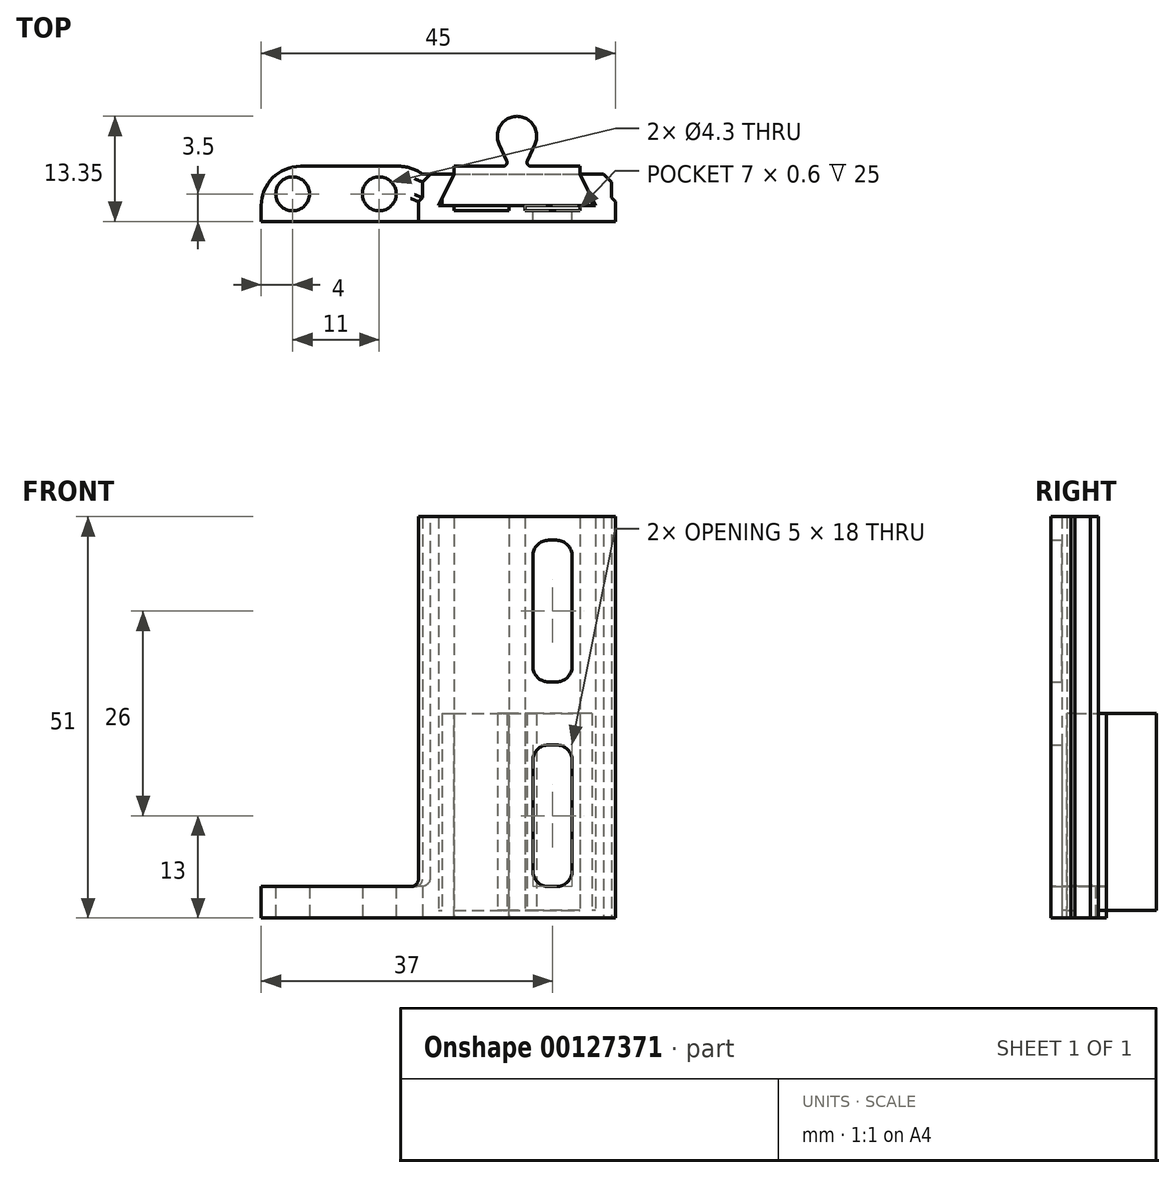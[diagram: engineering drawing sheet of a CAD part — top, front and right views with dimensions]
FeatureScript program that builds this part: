
annotation { "Feature Type Name" : "Feature", "Feature Type Description" : "" }
export const myFeature = defineFeature(function(context is Context, id is Id, definition is map)
    precondition{}
    {
        {
            var Q0;
            Q0=qCreatedBy(makeId("Top.planeOp"),FACE);
            var sketch = newSketch(context, id + "F0", { "sketchPlane" : qUnion([Q0])});
            skLineSegment(sketch, "E0.bottom", {"start": v(0, 0) * mm, "end": v(-2, 0) * mm});
            skLineSegment(sketch, "E0.top", {"start": v(0, -4) * mm, "end": v(-2, -4) * mm, "construction": true});
            skLineSegment(sketch, "E0.left", {"start": v(0, 0) * mm, "end": v(0, -4) * mm, "construction": true});
            skLineSegment(sketch, "E0.right", {"start": v(-2, 0) * mm, "end": v(-2, -4) * mm, "construction": true});
            skLineSegment(sketch, "E1", {"start": v(0, -4) * mm, "end": v(-2, 0) * mm});
            skLineSegment(sketch, "E2.bottom", {"start": v(0, 0) * mm, "end": v(2, 0) * mm});
            skLineSegment(sketch, "E2.top", {"start": v(0, -4) * mm, "end": v(2, -4) * mm});
            skLineSegment(sketch, "E2.right", {"start": v(2, 0) * mm, "end": v(2, -4) * mm});
            skLineSegment(sketch, "E3", {"start": v(-10, 5.55) * mm, "end": v(-10, -8.29) * mm, "construction": true});
            skLineSegment(sketch, "E4.MirrorCS", {"start": v(-20, -4) * mm, "end": v(-18, 0) * mm});
            skLineSegment(sketch, "E5.MirrorCS", {"start": v(-20, 0) * mm, "end": v(-18, 0) * mm});
            skLineSegment(sketch, "E6.MirrorCS", {"start": v(-20, 0) * mm, "end": v(-22, 0) * mm});
            skLineSegment(sketch, "E7.MirrorCS", {"start": v(-22, 0) * mm, "end": v(-22, -4) * mm});
            skLineSegment(sketch, "E8.MirrorCS", {"start": v(-20, -4) * mm, "end": v(-22, -4) * mm});
            skLineSegment(sketch, "E9.bottom", {"start": v(-22.5, -4) * mm, "end": v(2.5, -4) * mm});
            skLineSegment(sketch, "E9.top", {"start": v(-22.5, -6) * mm, "end": v(2.5, -6) * mm});
            skLineSegment(sketch, "E9.left", {"start": v(-22.5, -4) * mm, "end": v(-22.5, -6) * mm});
            skLineSegment(sketch, "E9.right", {"start": v(2.5, -4) * mm, "end": v(2.5, -6) * mm});
            skLineSegment(sketch, "E10", {"start": v(-10, -4) * mm, "end": v(-10, -6) * mm, "construction": true});
            skLineSegment(sketch, "E11", {"start": v(-18, 0) * mm, "end": v(-2, 0) * mm});
            skLineSegment(sketch, "E12.top", {"start": v(-18, 1) * mm, "end": v(-11.78, 1) * mm});
            skLineSegment(sketch, "E12.left", {"start": v(-18, 0) * mm, "end": v(-18, 1) * mm});
            skLineSegment(sketch, "E12.right", {"start": v(-2, 0) * mm, "end": v(-2, 1) * mm});
            skCircle(sketch, "E13", {"center": v(-10, 4.85) * mm, "radius": 2.5 * mm});
            skLineSegment(sketch, "E14", {"start": v(-11.32, 1.7) * mm, "end": v(-12.28, 3.81) * mm});
            skPoint(sketch, "E15.newPointA", {"position": v(-11, 1) * mm});
            skPoint(sketch, "E15.newPointB", {"position": v(-2, 1) * mm});
            skArc(sketch, "E15.filletArc", {"start": v(-11.78, 1) * mm, "mid": v(-11.36, 1.23) * mm, "end": v(-11.32, 1.7) * mm});
            skLineSegment(sketch, "E16.MirrorCS", {"start": v(-8.68, 1.7) * mm, "end": v(-7.72, 3.81) * mm});
            skArc(sketch, "E17.MirrorCS", {"start": v(-8.22, 1) * mm, "mid": v(-8.64, 1.23) * mm, "end": v(-8.68, 1.7) * mm});
            skLineSegment(sketch, "E18.MirrorCS", {"start": v(-2, 1) * mm, "end": v(-8.22, 1) * mm});
            skLineSegment(sketch, "E19", {"start": v(-0.5, -3) * mm, "end": v(-0.5, -4) * mm});
            skLineSegment(sketch, "E20.MirrorCS", {"start": v(-19.5, -3) * mm, "end": v(-19.5, -4) * mm});
            skLineSegment(sketch, "E21.bottom", {"start": v(-18, -4) * mm, "end": v(-11, -4) * mm});
            skLineSegment(sketch, "E21.top", {"start": v(-18, -4.6) * mm, "end": v(-11, -4.6) * mm});
            skLineSegment(sketch, "E21.left", {"start": v(-18, -4) * mm, "end": v(-18, -4.6) * mm});
            skLineSegment(sketch, "E21.right", {"start": v(-11, -4) * mm, "end": v(-11, -4.6) * mm});
            skLineSegment(sketch, "E22.MirrorCS", {"start": v(-9, -4) * mm, "end": v(-9, -4.6) * mm});
            skLineSegment(sketch, "E23.MirrorCS", {"start": v(-2, -4.6) * mm, "end": v(-9, -4.6) * mm});
            skLineSegment(sketch, "E24.MirrorCS", {"start": v(-2, -4) * mm, "end": v(-2, -4.6) * mm});
            skLineSegment(sketch, "E25", {"start": v(-22.5, -6) * mm, "end": v(-42.5, -6) * mm});
            skLineSegment(sketch, "E26", {"start": v(-42.5, -6) * mm, "end": v(-42.5, 1) * mm});
            skLineSegment(sketch, "E27", {"start": v(-42.5, 1) * mm, "end": v(-22, 1) * mm});
            skLineSegment(sketch, "E28", {"start": v(-22, 1) * mm, "end": v(-22, 0) * mm});
            skCircle(sketch, "E29", {"center": v(-38.5, -2.5) * mm, "radius": 2.15 * mm});
            skPoint(sketch, "E29.centerSnap0", {"position": v(-42.5, -2.5) * mm});
            skCircle(sketch, "E30", {"center": v(-27.5, -2.5) * mm, "radius": 2.15 * mm});
            skSolve(sketch);
        }
        {
            var Q0;
            Q0=makeQuery(id+"F0.imprint","IMPRINT",FACE,{"disambiguationData":[TD([[makeQuery(id+"F0.imprint","IMPRINT",EDGE,{"derivedFrom":sQuery(id+"F0.wireOp",EDGE,"E0.bottom")}),1.0]])]});
            var Q1;
            {var subQ1=sQuery(id+"F0.wireOp",EDGE,"E4.MirrorCS");Q1=makeQuery(id+"F0.imprint","IMPRINT",FACE,{"disambiguationData":[TD([[makeQuery(id+"F0.imprint","IMPRINT",EDGE,{"derivedFrom":subQ1}),1.0]])]});}
            var Q2;
            Q2=makeQuery(id+"F0.imprint","IMPRINT",FACE,{"disambiguationData":[TD([[makeQuery(id+"F0.imprint","IMPRINT",EDGE,{"derivedFrom":sQuery(id+"F0.wireOp",EDGE,"E9.top")}),1.0]])]});
            extrude(context, id + "F1", {"entities" : qUnion([Q0, Q1, Q2]), "depth" : 50 * mm});
        }
        {
            var Q0;
            {var subQ1=sQuery(id+"F0.wireOp",EDGE,"E0.bottom");Q0=makeQuery(id+"F0.imprint","IMPRINT",FACE,{"disambiguationData":[TD([[makeQuery(id+"F0.imprint","IMPRINT",EDGE,{"derivedFrom":subQ1}),1.0]])]});}
            var Q1;
            Q1=makeQuery(id+"F1.opExtrude","CAP_FACE",FACE,{"disambiguationData":[OSD([sQuery(id+"F0.wireOp",EDGE,"E0.bottom"),sQuery(id+"F0.wireOp",EDGE,"E1"),sQuery(id+"F0.wireOp",EDGE,"E2.bottom"),sQuery(id+"F0.wireOp",EDGE,"E2.right"),sQuery(id+"F0.wireOp",EDGE,"E4.MirrorCS"),sQuery(id+"F0.wireOp",EDGE,"E5.MirrorCS"),sQuery(id+"F0.wireOp",EDGE,"E6.MirrorCS"),sQuery(id+"F0.wireOp",EDGE,"E7.MirrorCS"),sQuery(id+"F0.wireOp",EDGE,"E9.bottom"),sQuery(id+"F0.wireOp",EDGE,"E9.top"),sQuery(id+"F0.wireOp",EDGE,"E9.left"),sQuery(id+"F0.wireOp",EDGE,"E9.right")])],"isStart":true});
            var Q2;
            {var subQ0=sQuery(id+"F0.wireOp",EDGE,"E11");Q2=makeQuery(id+"F0.imprint","IMPRINT",FACE,{"disambiguationData":[TD([[makeQuery(id+"F0.imprint","IMPRINT",EDGE,{"derivedFrom":subQ0}),-1.0]])]});}
            var Q3;
            {var subQ3=sQuery(id+"F0.wireOp",EDGE,"E19");Q3=makeQuery(id+"F0.imprint","IMPRINT",FACE,{"disambiguationData":[TD([[makeQuery(id+"F0.imprint","IMPRINT",EDGE,{"derivedFrom":subQ3}),1.0]])]});}
            var Q4;
            {var subQ3=sQuery(id+"F0.wireOp",EDGE,"E20.MirrorCS");Q4=makeQuery(id+"F0.imprint","IMPRINT",FACE,{"disambiguationData":[TD([[makeQuery(id+"F0.imprint","IMPRINT",EDGE,{"derivedFrom":subQ3}),-1.0]])]});}
            var Q5;
            {var subQ0=sQuery(id+"F0.wireOp",EDGE,"E22.MirrorCS");Q5=makeQuery(id+"F0.imprint","IMPRINT",FACE,{"disambiguationData":[TD([[makeQuery(id+"F0.imprint","IMPRINT",EDGE,{"derivedFrom":subQ0}),1.0]])]});}
            var Q6;
            Q6=makeQuery(id+"F0.imprint","IMPRINT",FACE,{"disambiguationData":[TD([[makeQuery(id+"F0.imprint","IMPRINT",EDGE,{"derivedFrom":sQuery(id+"F0.wireOp",EDGE,"E21.bottom")}),-1.0]])]});
            extrude(context, id + "F2", {"entities" : qUnion([Q0, Q1, Q2, Q3, Q4, Q5, Q6]), "operationType" : NewBodyOperationType.ADD, "oppositeDirection" : true, "depth" : 1 * mm});
        }
        {
            var Q0;
            Q0=makeQuery(id+"F1.opExtrude","SWEPT_EDGE",EDGE,{"disambiguationData":[OSD([sQuery(id+"F0.wireOp",EDGE,"E7.MirrorCS"),sQuery(id+"F0.wireOp",EDGE,"E9.bottom")])]});
            var Q1;
            Q1=makeQuery(id+"F1.opExtrude","SWEPT_EDGE",EDGE,{"disambiguationData":[OSD([sQuery(id+"F0.wireOp",EDGE,"E2.right"),sQuery(id+"F0.wireOp",EDGE,"E9.bottom")])]});
            var Q2;
            Q2=makeQuery(id+"F1.opExtrude","SWEPT_EDGE",EDGE,{"disambiguationData":[OSD([sQuery(id+"F0.wireOp",EDGE,"E6.MirrorCS"),sQuery(id+"F0.wireOp",EDGE,"E7.MirrorCS")])]});
            var Q3;
            Q3=makeQuery(id+"F1.opExtrude","SWEPT_EDGE",EDGE,{"disambiguationData":[OSD([sQuery(id+"F0.wireOp",EDGE,"E2.bottom"),sQuery(id+"F0.wireOp",EDGE,"E2.right")])]});
            chamfer(context, id + "F3", {"entities" : qUnion([Q0, Q1, Q2, Q3]), "width" : 1 * mm, "tangentPropagation" : true});
        }
        {
            var Q0;
            {var subQ0=sQuery(id+"F0.wireOp",EDGE,"E9.bottom");Q0=makeQuery(id+"F1.opExtrude","SWEPT_FACE",FACE,{"disambiguationData":[OSD([subQ0]),TDD([makeQuery(id+"F0.imprint","IMPRINT",EDGE,{"disambiguationData":[TD([[makeQuery(id+"F0.imprint","INTERSECT",VERTEX,{"derivedFrom":[sQuery(id+"F0.wireOp",EDGE,"E1"),subQ0]}),1.0]])],"derivedFrom":subQ0})])]});}
            var sketch = newSketch(context, id + "F4", { "sketchPlane" : qUnion([Q0])});
            skLineSegment(sketch, "E31.bottom", {"start": v(6, 47) * mm, "end": v(5, 47) * mm});
            skLineSegment(sketch, "E31.top", {"start": v(6, 29) * mm, "end": v(5, 29) * mm});
            skLineSegment(sketch, "E31.left", {"start": v(8, 45) * mm, "end": v(8, 31) * mm});
            skLineSegment(sketch, "E31.right", {"start": v(3, 45) * mm, "end": v(3, 31) * mm});
            skPoint(sketch, "E32.visualSharp", {"position": v(3, 47) * mm});
            skArc(sketch, "E32.filletArc", {"start": v(5, 47) * mm, "mid": v(3.59, 46.41) * mm, "end": v(3, 45) * mm});
            skPoint(sketch, "E33.visualSharp", {"position": v(3, 29) * mm});
            skArc(sketch, "E33.filletArc", {"start": v(3, 31) * mm, "mid": v(3.59, 29.59) * mm, "end": v(5, 29) * mm});
            skPoint(sketch, "E34.visualSharp", {"position": v(8, 29) * mm});
            skArc(sketch, "E34.filletArc", {"start": v(6, 29) * mm, "mid": v(7.41, 29.59) * mm, "end": v(8, 31) * mm});
            skPoint(sketch, "E35.visualSharp", {"position": v(8, 47) * mm});
            skArc(sketch, "E35.filletArc", {"start": v(8, 45) * mm, "mid": v(7.41, 46.41) * mm, "end": v(6, 47) * mm});
            skLineSegment(sketch, "E36", {"start": v(5.5, 29) * mm, "end": v(5.5, 34.69) * mm, "construction": true});
            skLineSegment(sketch, "E37", {"start": v(20, 25) * mm, "end": v(7.35, 25) * mm, "construction": true});
            skPoint(sketch, "E37.endSnap0", {"position": v(20, 25) * mm});
            skLineSegment(sketch, "E38.MirrorCS", {"start": v(6, 21) * mm, "end": v(5, 21) * mm});
            skArc(sketch, "E39.MirrorCS", {"start": v(6, 21) * mm, "mid": v(7.41, 20.41) * mm, "end": v(8, 19) * mm});
            skLineSegment(sketch, "E40.MirrorCS", {"start": v(8, 5) * mm, "end": v(8, 19) * mm});
            skArc(sketch, "E41.MirrorCS", {"start": v(8, 5) * mm, "mid": v(7.41, 3.59) * mm, "end": v(6, 3) * mm});
            skLineSegment(sketch, "E42.MirrorCS", {"start": v(6, 3) * mm, "end": v(5, 3) * mm});
            skArc(sketch, "E43.MirrorCS", {"start": v(5, 3) * mm, "mid": v(3.59, 3.59) * mm, "end": v(3, 5) * mm});
            skLineSegment(sketch, "E44.MirrorCS", {"start": v(3, 5) * mm, "end": v(3, 19) * mm});
            skArc(sketch, "E45.MirrorCS", {"start": v(3, 19) * mm, "mid": v(3.59, 20.41) * mm, "end": v(5, 21) * mm});
            skLineSegment(sketch, "E46.0", {"start": v(2, 50) * mm, "end": v(9, 50) * mm});
            skLineSegment(sketch, "E47", {"start": v(5.5, 50) * mm, "end": v(5.5, 26.66) * mm, "construction": true});
            skSolve(sketch);
        }
        {
            var Q0;
            Q0=makeQuery(id+"F4.imprint","IMPRINT",FACE,{"disambiguationData":[TD([[makeQuery(id+"F4.imprint","IMPRINT",EDGE,{"derivedFrom":sQuery(id+"F4.wireOp",EDGE,"E31.bottom")}),1.0]])]});
            var Q1;
            Q1=makeQuery(id+"F4.imprint","IMPRINT",FACE,{"disambiguationData":[TD([[makeQuery(id+"F4.imprint","IMPRINT",EDGE,{"derivedFrom":sQuery(id+"F4.wireOp",EDGE,"E38.MirrorCS")}),1.0]])]});
            extrude(context, id + "F5", {"entities" : qUnion([Q0, Q1]), "operationType" : NewBodyOperationType.REMOVE, "oppositeDirection" : true, "depth" : 25 * mm});
        }
        {
            var Q0;
            {var subQ0=sQuery(id+"F0.wireOp",EDGE,"E13");var subQ1=makeQuery(id+"F0.imprint","INTERSECT",VERTEX,{"derivedFrom":[subQ0,sQuery(id+"F0.wireOp",EDGE,"E14")]});Q0=makeQuery(id+"F0.imprint","IMPRINT",FACE,{"disambiguationData":[TD([[makeQuery(id+"F0.imprint","IMPRINT",EDGE,{"disambiguationData":[TD([[subQ1,-1.0]])],"derivedFrom":subQ0}),1.0]])]});}
            var Q1;
            Q1=makeQuery(id+"F0.imprint","IMPRINT",FACE,{"disambiguationData":[TD([[makeQuery(id+"F0.imprint","IMPRINT",EDGE,{"derivedFrom":sQuery(id+"F0.wireOp",EDGE,"E11")}),1.0]])]});
            var Q2;
            {var subQ0=sQuery(id+"F0.wireOp",EDGE,"E11");Q2=makeQuery(id+"F0.imprint","IMPRINT",FACE,{"disambiguationData":[TD([[makeQuery(id+"F0.imprint","IMPRINT",EDGE,{"derivedFrom":subQ0}),-1.0]])]});}
            extrude(context, id + "F6", {"entities" : qUnion([Q0, Q1, Q2]), "depth" : 25 * mm});
        }
        {
            var Q0;
            {var subQ2=sQuery(id+"F0.wireOp",EDGE,"E7.MirrorCS");Q0=makeQuery(id+"F0.imprint","IMPRINT",FACE,{"disambiguationData":[TD([[makeQuery(id+"F0.imprint","IMPRINT",EDGE,{"derivedFrom":subQ2}),-1.0]])]});}
            var Q1;
            {var subQ0=sQuery(id+"F0.wireOp",EDGE,"E5.MirrorCS");Q1=makeQuery(id+"F0.imprint","IMPRINT",FACE,{"disambiguationData":[TD([[makeQuery(id+"F0.imprint","IMPRINT",EDGE,{"derivedFrom":subQ0}),-1.0]])]});}
            extrude(context, id + "F7", {"entities" : qUnion([Q0, Q1]), "operationType" : NewBodyOperationType.ADD, "depth" : 3 * mm, "hasSecondDirection" : true, "secondDirectionOppositeDirection" : true, "secondDirectionDepth" : 1 * mm});
        }
        {
            var Q0;
            {var subQ0=sQuery(id+"F0.wireOp",EDGE,"E9.left");Q0=makeQuery(id+"F7.boolean.opBoolean","INTERSECT",EDGE,{"derivedFrom":[makeQuery(id+"F2.boolean.opBoolean","MERGE",FACE,{"derivedFrom":[makeQuery(id+"F1.opExtrude","SWEPT_FACE",FACE,{"disambiguationData":[OSD([subQ0])]}),makeQuery(id+"F2.opExtrude","SWEPT_FACE",FACE,{"disambiguationData":[OSD([subQ0])]})]}),makeQuery(id+"F7.opExtrude","CAP_FACE",FACE,{"disambiguationData":[OSD([sQuery(id+"F0.wireOp",EDGE,"E4.MirrorCS"),sQuery(id+"F0.wireOp",EDGE,"E5.MirrorCS"),sQuery(id+"F0.wireOp",EDGE,"E6.MirrorCS"),sQuery(id+"F0.wireOp",EDGE,"E9.bottom"),subQ0,sQuery(id+"F0.wireOp",EDGE,"E25"),sQuery(id+"F0.wireOp",EDGE,"E26"),sQuery(id+"F0.wireOp",EDGE,"E27"),sQuery(id+"F0.wireOp",EDGE,"E28"),sQuery(id+"F0.wireOp",EDGE,"E29"),sQuery(id+"F0.wireOp",EDGE,"E30")])],"isStart":false})]});}
            var Q1;
            {var subQ0=sQuery(id+"F0.wireOp",EDGE,"E9.bottom");Q1=makeQuery(id+"F7.boolean.opBoolean","INTERSECT",EDGE,{"derivedFrom":[makeQuery(id+"F3.opChamfer","BLEND_FACE",FACE,{"disambiguationData":[OSD([sQuery(id+"F0.wireOp",EDGE,"E7.MirrorCS"),subQ0])]}),makeQuery(id+"F7.opExtrude","CAP_FACE",FACE,{"disambiguationData":[OSD([sQuery(id+"F0.wireOp",EDGE,"E4.MirrorCS"),sQuery(id+"F0.wireOp",EDGE,"E5.MirrorCS"),sQuery(id+"F0.wireOp",EDGE,"E6.MirrorCS"),subQ0,sQuery(id+"F0.wireOp",EDGE,"E9.left"),sQuery(id+"F0.wireOp",EDGE,"E25"),sQuery(id+"F0.wireOp",EDGE,"E26"),sQuery(id+"F0.wireOp",EDGE,"E27"),sQuery(id+"F0.wireOp",EDGE,"E28"),sQuery(id+"F0.wireOp",EDGE,"E29"),sQuery(id+"F0.wireOp",EDGE,"E30")])],"isStart":false})]});}
            var Q2;
            {var subQ0=sQuery(id+"F0.wireOp",EDGE,"E7.MirrorCS");Q2=makeQuery(id+"F7.boolean.opBoolean","INTERSECT",EDGE,{"derivedFrom":[makeQuery(id+"F2.boolean.opBoolean","MERGE",FACE,{"derivedFrom":[makeQuery(id+"F1.opExtrude","SWEPT_FACE",FACE,{"disambiguationData":[OSD([subQ0])]}),makeQuery(id+"F2.opExtrude","SWEPT_FACE",FACE,{"disambiguationData":[OSD([subQ0])]})]}),makeQuery(id+"F7.opExtrude","CAP_FACE",FACE,{"disambiguationData":[OSD([sQuery(id+"F0.wireOp",EDGE,"E4.MirrorCS"),sQuery(id+"F0.wireOp",EDGE,"E5.MirrorCS"),sQuery(id+"F0.wireOp",EDGE,"E6.MirrorCS"),sQuery(id+"F0.wireOp",EDGE,"E9.bottom"),sQuery(id+"F0.wireOp",EDGE,"E9.left"),sQuery(id+"F0.wireOp",EDGE,"E25"),sQuery(id+"F0.wireOp",EDGE,"E26"),sQuery(id+"F0.wireOp",EDGE,"E27"),sQuery(id+"F0.wireOp",EDGE,"E28"),sQuery(id+"F0.wireOp",EDGE,"E29"),sQuery(id+"F0.wireOp",EDGE,"E30")])],"isStart":false})]});}
            var Q3;
            {var subQ0=sQuery(id+"F0.wireOp",EDGE,"E28");var subQ1=sQuery(id+"F0.wireOp",EDGE,"E6.MirrorCS");Q3=makeQuery(id+"F7.boolean.opBoolean","INTERSECT",EDGE,{"derivedFrom":[makeQuery(id+"F3.opChamfer","BLEND_FACE",FACE,{"disambiguationData":[OSD([subQ1,sQuery(id+"F0.wireOp",EDGE,"E7.MirrorCS"),subQ0])]}),makeQuery(id+"F7.opExtrude","CAP_FACE",FACE,{"disambiguationData":[OSD([sQuery(id+"F0.wireOp",EDGE,"E4.MirrorCS"),sQuery(id+"F0.wireOp",EDGE,"E5.MirrorCS"),subQ1,sQuery(id+"F0.wireOp",EDGE,"E9.bottom"),sQuery(id+"F0.wireOp",EDGE,"E9.left"),sQuery(id+"F0.wireOp",EDGE,"E25"),sQuery(id+"F0.wireOp",EDGE,"E26"),sQuery(id+"F0.wireOp",EDGE,"E27"),subQ0,sQuery(id+"F0.wireOp",EDGE,"E29"),sQuery(id+"F0.wireOp",EDGE,"E30")])],"isStart":false})]});}
            fillet(context, id + "F8", {"entities" : qUnion([Q0, Q1, Q2, Q3]), "radius" : 1 * mm, "tangentPropagation" : true, "allowEdgeOverflow" : false});
        }
        {
            var Q0;
            Q0=makeQuery(id+"F7.opExtrude","SWEPT_EDGE",EDGE,{"disambiguationData":[OSD([sQuery(id+"F0.wireOp",EDGE,"E27"),sQuery(id+"F0.wireOp",EDGE,"E28")])]});
            var Q1;
            Q1=makeQuery(id+"F7.opExtrude","SWEPT_EDGE",EDGE,{"disambiguationData":[OSD([sQuery(id+"F0.wireOp",EDGE,"E26"),sQuery(id+"F0.wireOp",EDGE,"E27")])]});
            fillet(context, id + "F9", {"entities" : qUnion([Q0, Q1]), "radius" : 5 * mm, "tangentPropagation" : true, "allowEdgeOverflow" : false});
        }
    });
